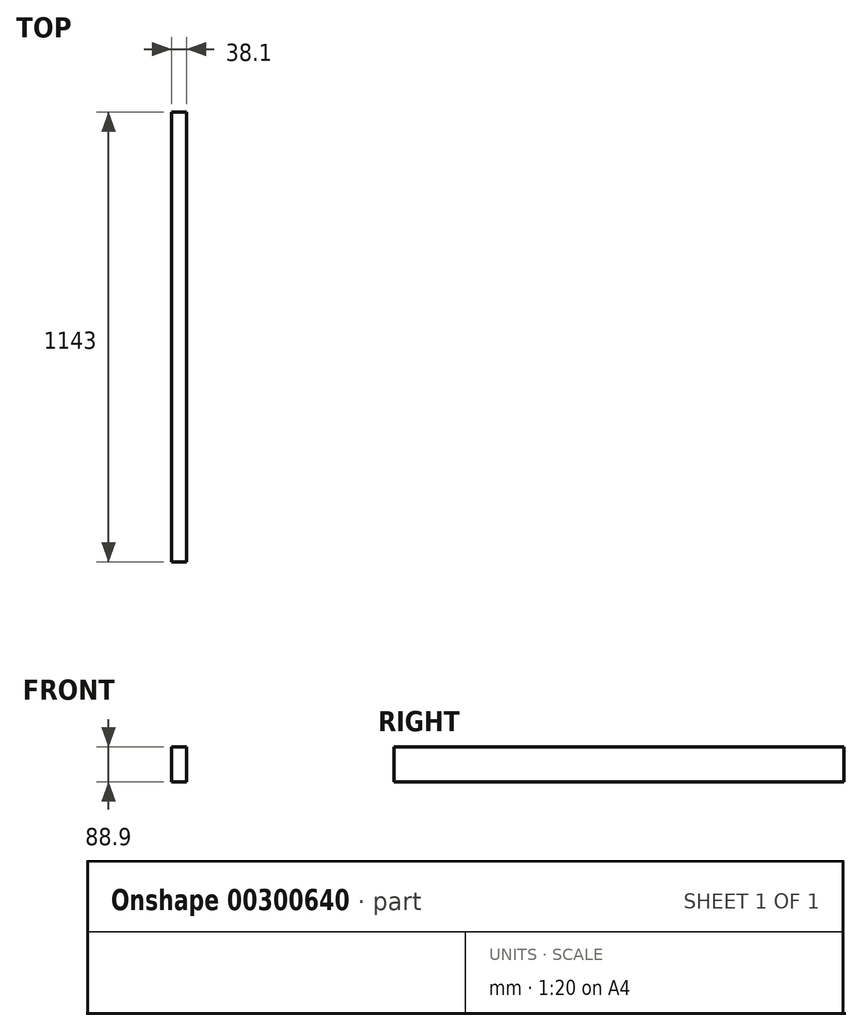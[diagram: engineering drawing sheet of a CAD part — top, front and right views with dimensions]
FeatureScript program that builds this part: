
annotation { "Feature Type Name" : "Feature", "Feature Type Description" : "" }
export const myFeature = defineFeature(function(context is Context, id is Id, definition is map)
    precondition{}
    {
        {
            var Q0;
            Q0=qCreatedBy(makeId("Front.planeOp"),FACE);
            var sketch = newSketch(context, id + "F0", { "sketchPlane" : qUnion([Q0])});
            skLineSegment(sketch, "E0.bottom", {"start": v(19.05, 44.45) * mm, "end": v(-19.05, 44.45) * mm});
            skLineSegment(sketch, "E0.top", {"start": v(19.05, -44.45) * mm, "end": v(-19.05, -44.45) * mm});
            skLineSegment(sketch, "E0.left", {"start": v(19.05, 44.45) * mm, "end": v(19.05, -44.45) * mm});
            skLineSegment(sketch, "E0.right", {"start": v(-19.05, 44.45) * mm, "end": v(-19.05, -44.45) * mm});
            skPoint(sketch, "E0.middle", {"position": v(0, 0) * mm});
            skSolve(sketch);
        }
        {
            var Q0;
            Q0=qSketchRegion(id+"F0",true);
            extrude(context, id + "F1", {"entities" : qUnion([Q0]), "oppositeDirection" : true, "depth" : 1143 * mm});
        }
    });
